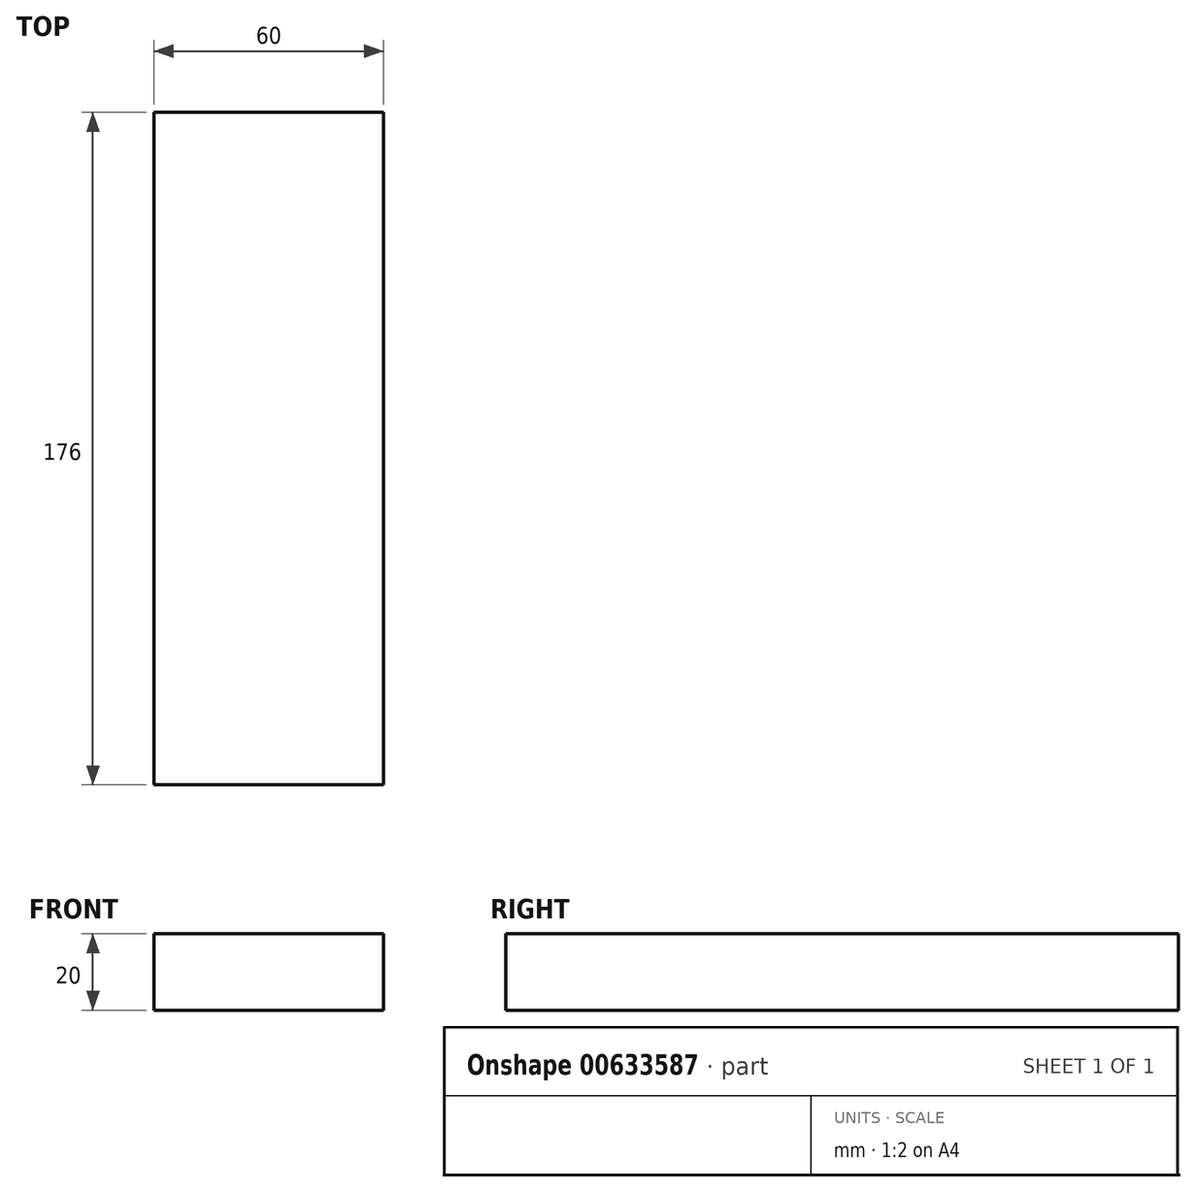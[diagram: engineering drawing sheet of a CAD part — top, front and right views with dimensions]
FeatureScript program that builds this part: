
annotation { "Feature Type Name" : "Feature", "Feature Type Description" : "" }
export const myFeature = defineFeature(function(context is Context, id is Id, definition is map)
    precondition{}
    {
        {
            var Q0;
            Q0=qCreatedBy(makeId("Top.planeOp"),FACE);
            var sketch = newSketch(context, id + "F0", { "sketchPlane" : qUnion([Q0])});
            skLineSegment(sketch, "E0", {"start": v(-30, 17.32) * mm, "end": v(30, 17.32) * mm});
            skLineSegment(sketch, "E1", {"start": v(30, 17.32) * mm, "end": v(0, -34.64) * mm, "construction": true});
            skLineSegment(sketch, "E2", {"start": v(0, -34.64) * mm, "end": v(-30, 17.32) * mm, "construction": true});
            skCircle(sketch, "E3", {"center": v(0, 0) * mm, "radius": 34.64 * mm, "construction": true});
            skLineSegment(sketch, "E4.bottom", {"start": v(-30, 193.32) * mm, "end": v(30, 193.32) * mm});
            skLineSegment(sketch, "E4.left", {"start": v(-30, 193.32) * mm, "end": v(-30, 17.32) * mm});
            skLineSegment(sketch, "E4.right", {"start": v(30, 193.32) * mm, "end": v(30, 17.32) * mm});
            skPoint(sketch, "E4.middle", {"position": v(0, 105.32) * mm});
            skLineSegment(sketch, "E5.bottom", {"start": v(-30, 193.32) * mm, "end": v(30, 193.32) * mm, "construction": true});
            skLineSegment(sketch, "E5.top", {"start": v(-30, 213.32) * mm, "end": v(30, 213.32) * mm, "construction": true});
            skLineSegment(sketch, "E5.left", {"start": v(-30, 193.32) * mm, "end": v(-30, 213.32) * mm, "construction": true});
            skLineSegment(sketch, "E5.right", {"start": v(30, 193.32) * mm, "end": v(30, 213.32) * mm, "construction": true});
            skPoint(sketch, "E5.middle", {"position": v(0, 203.32) * mm});
            skCircle(sketch, "E6", {"center": v(0, 0) * mm, "radius": 195.63 * mm, "construction": true});
            skLineSegment(sketch, "E7", {"start": v(-30, 179.82) * mm, "end": v(30, 179.82) * mm, "construction": true});
            skCircle(sketch, "E8", {"center": v(0, 0) * mm, "radius": 150 * mm, "construction": true});
            skLineSegment(sketch, "E9", {"start": v(-30, 17.32) * mm, "end": v(-182.42, -70.68) * mm, "construction": true});
            skLineSegment(sketch, "E10", {"start": v(-182.42, -70.68) * mm, "end": v(-152.42, -122.64) * mm, "construction": true});
            skLineSegment(sketch, "E11", {"start": v(-152.42, -122.64) * mm, "end": v(0, -34.64) * mm, "construction": true});
            skLineSegment(sketch, "E12", {"start": v(0, -34.64) * mm, "end": v(152.42, -122.64) * mm, "construction": true});
            skLineSegment(sketch, "E13", {"start": v(152.42, -122.64) * mm, "end": v(182.42, -70.68) * mm, "construction": true});
            skLineSegment(sketch, "E14", {"start": v(182.42, -70.68) * mm, "end": v(30, 17.32) * mm, "construction": true});
            skLineSegment(sketch, "E15", {"start": v(-30, 193.32) * mm, "end": v(-182.42, -70.68) * mm, "construction": true});
            skLineSegment(sketch, "E16", {"start": v(-152.42, -122.64) * mm, "end": v(152.42, -122.64) * mm, "construction": true});
            skLineSegment(sketch, "E17", {"start": v(182.42, -70.68) * mm, "end": v(30, 193.32) * mm, "construction": true});
            skLineSegment(sketch, "E18.bottom", {"start": v(-199.74, 213.32) * mm, "end": v(199.74, 213.32) * mm, "construction": true});
            skLineSegment(sketch, "E18.top", {"start": v(-199.74, -132.64) * mm, "end": v(199.74, -132.64) * mm, "construction": true});
            skLineSegment(sketch, "E18.left", {"start": v(-199.74, 213.32) * mm, "end": v(-199.74, -132.64) * mm, "construction": true});
            skLineSegment(sketch, "E18.right", {"start": v(199.74, 213.32) * mm, "end": v(199.74, -132.64) * mm, "construction": true});
            skLineSegment(sketch, "E19", {"start": v(152.42, -122.64) * mm, "end": v(169.74, -132.64) * mm, "construction": true});
            skLineSegment(sketch, "E20", {"start": v(169.74, -132.64) * mm, "end": v(199.74, -80.68) * mm, "construction": true});
            skLineSegment(sketch, "E21", {"start": v(199.74, -80.68) * mm, "end": v(182.42, -70.68) * mm, "construction": true});
            skLineSegment(sketch, "E22", {"start": v(-199.74, -80.68) * mm, "end": v(-169.74, -132.64) * mm, "construction": true});
            skLineSegment(sketch, "E23", {"start": v(-169.74, -132.64) * mm, "end": v(-152.42, -122.64) * mm, "construction": true});
            skLineSegment(sketch, "E24", {"start": v(-199.74, -80.68) * mm, "end": v(-182.42, -70.68) * mm, "construction": true});
            skLineSegment(sketch, "E25", {"start": v(0, 193.32) * mm, "end": v(-167.42, -96.66) * mm, "construction": true});
            skLineSegment(sketch, "E26", {"start": v(-167.42, -96.66) * mm, "end": v(167.42, -96.66) * mm, "construction": true});
            skLineSegment(sketch, "E27", {"start": v(167.42, -96.66) * mm, "end": v(0, 193.32) * mm, "construction": true});
            skCircle(sketch, "E28", {"center": v(0, 150) * mm, "radius": 27 * mm, "construction": true});
            skLineSegment(sketch, "E29", {"start": v(-54, 169.84) * mm, "end": v(-54, 112.13) * mm, "construction": true});
            skLineSegment(sketch, "E30", {"start": v(-68.75, 153.32) * mm, "end": v(-11.19, 153.32) * mm, "construction": true});
            skSolve(sketch);
        }
        {
            var Q0;
            Q0=makeQuery(id+"F0.imprint","IMPRINT",FACE,{"disambiguationData":[TD([[makeQuery(id+"F0.imprint","IMPRINT",EDGE,{"derivedFrom":sQuery(id+"F0.wireOp",EDGE,"E4.bottom")}),-1.0]])]});
            extrude(context, id + "F1", {"entities" : qUnion([Q0]), "depth" : 20 * mm});
        }
    });
